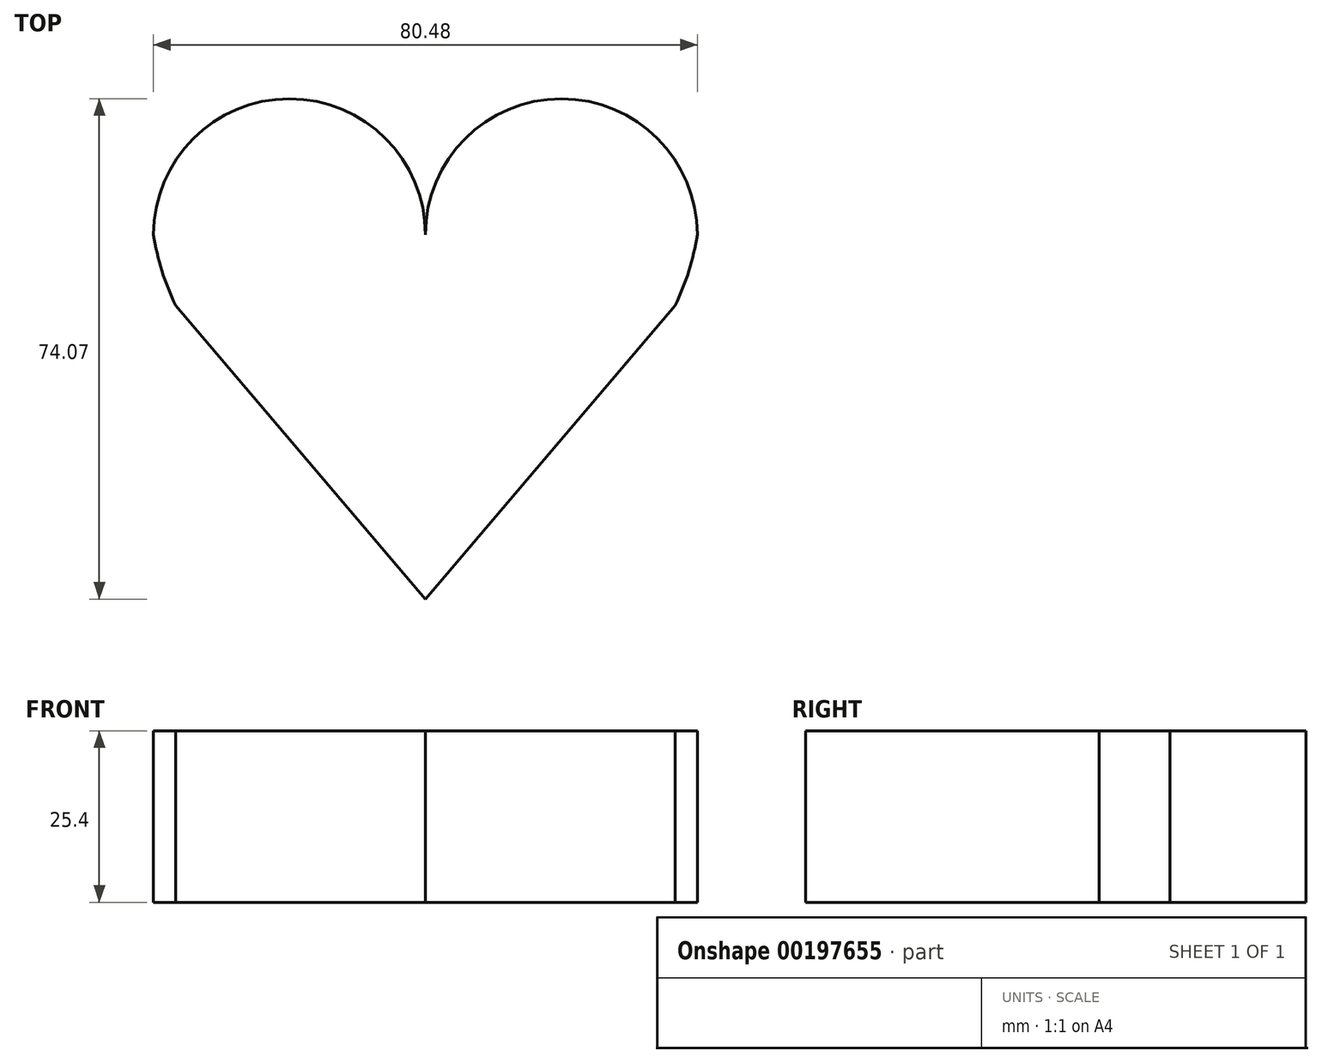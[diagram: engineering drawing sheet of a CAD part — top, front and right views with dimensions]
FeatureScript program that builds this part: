
annotation { "Feature Type Name" : "Feature", "Feature Type Description" : "" }
export const myFeature = defineFeature(function(context is Context, id is Id, definition is map)
    precondition{}
    {
        {
            var Q0;
            Q0=qCreatedBy(makeId("Top.planeOp"),FACE);
            var sketch = newSketch(context, id + "F0", { "sketchPlane" : qUnion([Q0])});
            skLineSegment(sketch, "E0", {"start": v(0, 0) * mm, "end": v(0, -2.41) * mm});
            skArc(sketch, "E1", {"start": v(0, 0) * mm, "mid": v(-20.12, 20.12) * mm, "end": v(-40.24, 0) * mm});
            skArc(sketch, "E2.MirrorCS", {"start": v(0, 0) * mm, "mid": v(20.12, 20.12) * mm, "end": v(40.24, 0) * mm});
            skArc(sketch, "E3", {"start": v(-0.07, 1.7) * mm, "mid": v(-0.14, -0.36) * mm, "end": v(0, -2.41) * mm});
            skLineSegment(sketch, "E4", {"start": v(-36.96, -10.47) * mm, "end": v(0, -53.95) * mm});
            skLineSegment(sketch, "E5.MirrorCS", {"start": v(31.75, -16.6) * mm, "end": v(0, -53.95) * mm});
            skPoint(sketch, "E6.orphan", {"position": v(40.24, 0) * mm});
            skPoint(sketch, "E7.MirrorCS.end.orphan", {"position": v(0, -53.95) * mm});
            skPoint(sketch, "E8.orphan", {"position": v(36.96, -10.47) * mm});
            skArc(sketch, "E9", {"start": v(-40.24, 0) * mm, "mid": v(-38.99, -5.36) * mm, "end": v(-36.96, -10.47) * mm});
            skArc(sketch, "E10.MirrorCS", {"start": v(40.24, 0) * mm, "mid": v(38.99, -5.36) * mm, "end": v(36.96, -10.47) * mm});
            skLineSegment(sketch, "E11.MirrorCS", {"start": v(36.96, -10.47) * mm, "end": v(0, -53.95) * mm});
            skSolve(sketch);
        }
        {
            var Q0;
            Q0 = qSketchRegion(id + "F0", true);
            var Q1;
            Q1=makeQuery(id+"F0.imprint","IMPRINT",FACE,{"disambiguationData":[TD([[makeQuery(id+"F0.imprint","IMPRINT",EDGE,{"derivedFrom":sQuery(id+"F0.wireOp",EDGE,"E0")}),1.0]])]});
            extrude(context, id + "F1", {"entities" : qUnion([Q0, Q1]), "depth" : 25.4 * mm});
        }
    });
